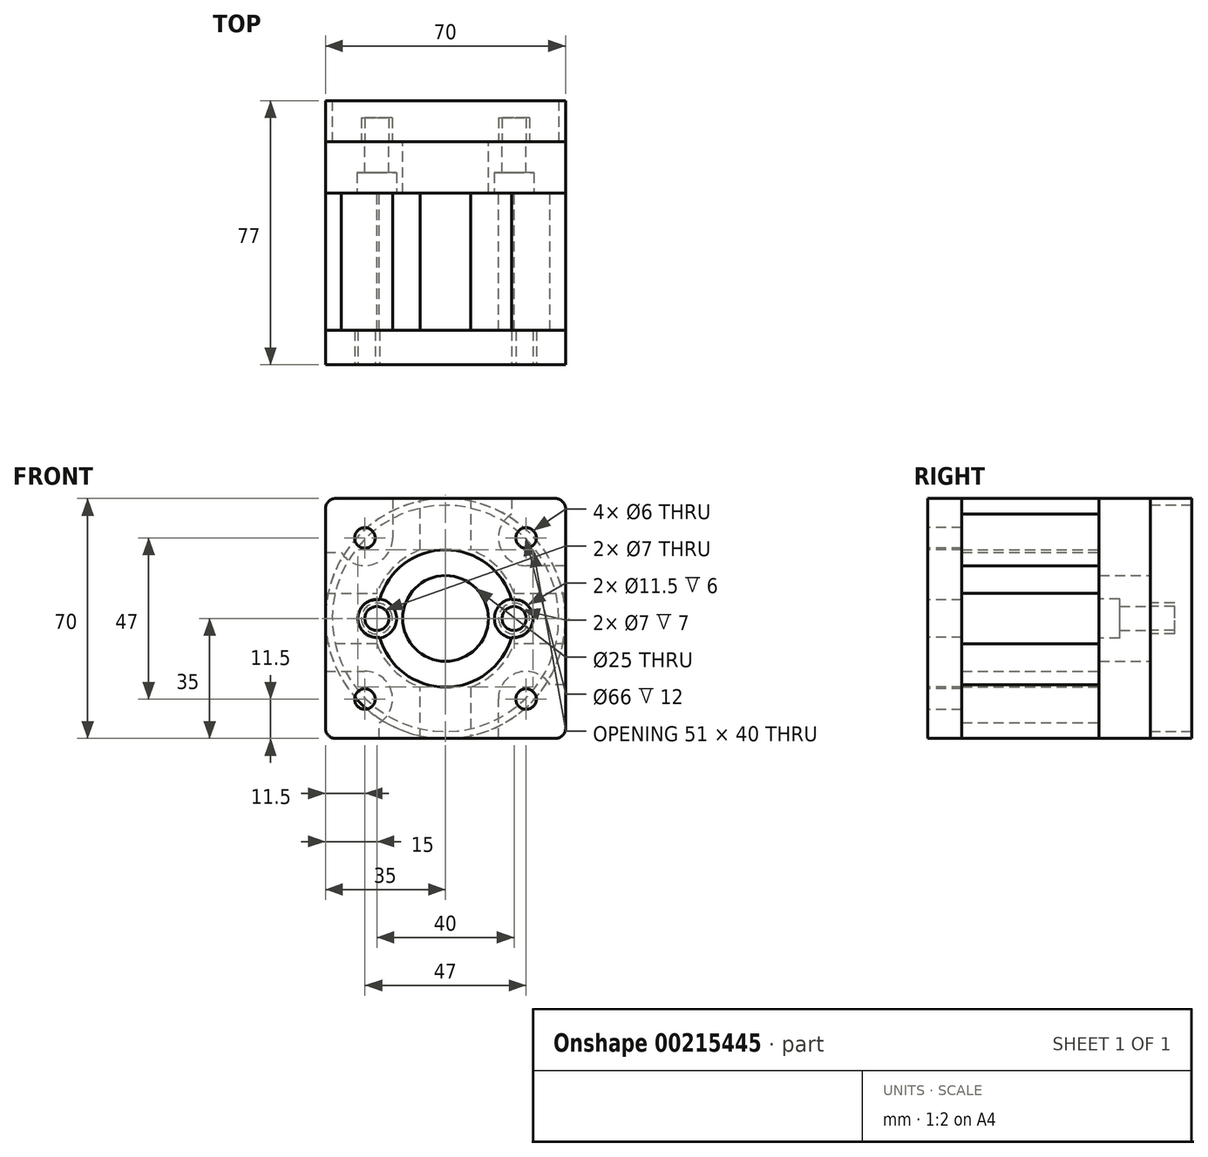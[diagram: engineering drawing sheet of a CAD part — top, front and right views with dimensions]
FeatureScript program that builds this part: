
annotation { "Feature Type Name" : "Feature", "Feature Type Description" : "" }
export const myFeature = defineFeature(function(context is Context, id is Id, definition is map)
    precondition{}
    {
        {
            var Q0;
            Q0=qCreatedBy(makeId("Front.planeOp"),FACE);
            var sketch = newSketch(context, id + "F0", { "sketchPlane" : qUnion([Q0])});
            skCircle(sketch, "E0", {"center": v(-20, 0) * mm, "radius": 4.5 * mm});
            skCircle(sketch, "E1", {"center": v(20, 0) * mm, "radius": 4.5 * mm});
            skCircle(sketch, "E2", {"center": v(-20, 0) * mm, "radius": 3.5 * mm});
            skCircle(sketch, "E3", {"center": v(20, 0) * mm, "radius": 3.5 * mm});
            skSolve(sketch);
        }
        {
            var Q0;
            Q0=makeQuery(id+"F0.imprint","IMPRINT",FACE,{"disambiguationData":[TD([[makeQuery(id+"F0.imprint","IMPRINT",EDGE,{"derivedFrom":sQuery(id+"F0.wireOp",EDGE,"E0")}),1.0]])]});
            var Q1;
            Q1=makeQuery(id+"F0.imprint","IMPRINT",FACE,{"disambiguationData":[TD([[makeQuery(id+"F0.imprint","IMPRINT",EDGE,{"derivedFrom":sQuery(id+"F0.wireOp",EDGE,"E1")}),1.0]])]});
            var Q2;
            Q2=sQuery(id+"F0.wireOp",EDGE,"E0");
            var Q3;
            Q3=sQuery(id+"F0.wireOp",EDGE,"E2");
            var Q4;
            Q4=sQuery(id+"F0.wireOp",EDGE,"E3");
            var Q5;
            Q5=sQuery(id+"F0.wireOp",EDGE,"E1");
            extrude(context, id + "F1", {"entities" : qUnion([Q0, Q1]), "surfaceEntities" : qUnion([Q2, Q3, Q4, Q5]), "oppositeDirection" : true, "depth" : 7 * mm});
        }
        {
            var Q0;
            Q0=qCreatedBy(makeId("Front.planeOp"),FACE);
            var sketch = newSketch(context, id + "F2", { "sketchPlane" : qUnion([Q0])});
            skCircle(sketch, "E4", {"center": v(0, 0) * mm, "radius": 35 * mm});
            skCircle(sketch, "E5", {"center": v(0, 0) * mm, "radius": 33 * mm});
            skSolve(sketch);
        }
        {
            var Q0;
            Q0=makeQuery(id+"F2.imprint","IMPRINT",FACE,{"disambiguationData":[TD([[makeQuery(id+"F2.imprint","IMPRINT",EDGE,{"derivedFrom":sQuery(id+"F2.wireOp",EDGE,"E4")}),1.0]])]});
            var Q1;
            Q1=sQuery(id+"F2.wireOp",EDGE,"E4");
            var Q2;
            Q2=sQuery(id+"F2.wireOp",EDGE,"E5");
            extrude(context, id + "F3", {"entities" : qUnion([Q0]), "surfaceEntities" : qUnion([Q1, Q2]), "oppositeDirection" : true, "depth" : 12 * mm});
        }
        {
            var Q0;
            Q0=qCreatedBy(makeId("Front.planeOp"),FACE);
            var sketch = newSketch(context, id + "F4", { "sketchPlane" : qUnion([Q0])});
            skLineSegment(sketch, "E6.bottom", {"start": v(-35, 35) * mm, "end": v(35, 35) * mm});
            skLineSegment(sketch, "E6.top", {"start": v(-35, -35) * mm, "end": v(35, -35) * mm});
            skLineSegment(sketch, "E6.left", {"start": v(-35, 35) * mm, "end": v(-35, -35) * mm});
            skLineSegment(sketch, "E6.right", {"start": v(35, 35) * mm, "end": v(35, -35) * mm});
            skCircle(sketch, "E7", {"center": v(0, 0) * mm, "radius": 12.5 * mm});
            skCircle(sketch, "E8", {"center": v(20, 0) * mm, "radius": 3.5 * mm});
            skCircle(sketch, "E9", {"center": v(-20, 0) * mm, "radius": 3.5 * mm});
            skSolve(sketch);
        }
        {
            var Q0;
            Q0=qSketchRegion(id+"F4",true);
            extrude(context, id + "F5", {"entities" : qUnion([Q0]), "depth" : 15 * mm});
        }
        {
            var Q0;
            Q0=qCreatedBy(makeId("Front.planeOp"),FACE);
            cPlane(context, id + "F6", {"entities" : qUnion([Q0]), "cplaneType" : CPlaneType.OFFSET, "offset" : 15 * mm, "width" : 150 * mm, "height" : 150 * mm});
        }
        {
            var Q0;
            Q0=qCreatedBy(id+"F6.planeOp",FACE);
            var sketch = newSketch(context, id + "F7", { "sketchPlane" : qUnion([Q0])});
            skCircle(sketch, "E10", {"center": v(-20, 0) * mm, "radius": 5.75 * mm});
            skCircle(sketch, "E11", {"center": v(20, 0) * mm, "radius": 5.75 * mm});
            skSolve(sketch);
        }
        {
            var Q0;
            Q0=qSketchRegion(id+"F7",true);
            extrude(context, id + "F8", {"entities" : qUnion([Q0]), "operationType" : NewBodyOperationType.REMOVE, "oppositeDirection" : true, "depth" : 6 * mm});
        }
        {
            var Q0;
            Q0=qCreatedBy(makeId("Front.planeOp"),FACE);
            cPlane(context, id + "F9", {"entities" : qUnion([Q0]), "cplaneType" : CPlaneType.OFFSET, "offset" : 65 * mm, "width" : 150 * mm, "height" : 150 * mm});
        }
        {
            var Q0;
            Q0=qCreatedBy(id+"F9.planeOp",FACE);
            var sketch = newSketch(context, id + "F10", { "sketchPlane" : qUnion([Q0])});
            skLineSegment(sketch, "E12.bottom", {"start": v(-35, 35) * mm, "end": v(35, 35) * mm});
            skLineSegment(sketch, "E12.top", {"start": v(-35, -35) * mm, "end": v(35, -35) * mm});
            skLineSegment(sketch, "E12.left", {"start": v(-35, 35) * mm, "end": v(-35, -35) * mm});
            skLineSegment(sketch, "E12.right", {"start": v(35, 35) * mm, "end": v(35, -35) * mm});
            skCircle(sketch, "E13", {"center": v(0, 0) * mm, "radius": 20 * mm});
            skCircle(sketch, "E14", {"center": v(-23.5, 23.5) * mm, "radius": 3 * mm});
            skCircle(sketch, "E15", {"center": v(23.5, 23.5) * mm, "radius": 3 * mm});
            skCircle(sketch, "E16", {"center": v(-23.5, -23.5) * mm, "radius": 3 * mm});
            skCircle(sketch, "E17", {"center": v(23.5, -23.5) * mm, "radius": 3 * mm});
            skCircle(sketch, "E18", {"center": v(-20, 0) * mm, "radius": 5.5 * mm});
            skCircle(sketch, "E19", {"center": v(20, 0) * mm, "radius": 5.5 * mm});
            skSolve(sketch);
        }
        {
            var Q0;
            Q0=qSketchRegion(id+"F10",true);
            extrude(context, id + "F11", {"entities" : qUnion([Q0]), "oppositeDirection" : true, "depth" : 10 * mm});
        }
        {
            var Q0;
            Q0=qCreatedBy(id+"F6.planeOp",FACE);
            var sketch = newSketch(context, id + "F12", { "sketchPlane" : qUnion([Q0])});
            skArc(sketch, "E20", {"start": v(-15.4, 23.5) * mm, "mid": v(-21.31, 15.7) * mm, "end": v(-30.4, 19.28) * mm});
            skLineSegment(sketch, "E21", {"start": v(-35, 19.28) * mm, "end": v(-30.4, 19.28) * mm});
            skPoint(sketch, "E22.center", {"position": v(0, 0) * mm});
            skLineSegment(sketch, "E23", {"start": v(-7.4, 20) * mm, "end": v(-7.4, 35) * mm});
            skLineSegment(sketch, "E24", {"start": v(-7.4, 35) * mm, "end": v(-15.4, 35) * mm});
            skLineSegment(sketch, "E25", {"start": v(-15.4, 35) * mm, "end": v(-15.4, 23.5) * mm});
            skLineSegment(sketch, "E26", {"start": v(-35, 7.4) * mm, "end": v(-20, 7.4) * mm});
            skLineSegment(sketch, "E27", {"start": v(-35, 19.28) * mm, "end": v(-35, 7.4) * mm});
            skArc(sketch, "E28", {"start": v(-7.4, 20) * mm, "mid": v(-15.07, 15.07) * mm, "end": v(-20, 7.4) * mm});
            skLineSegment(sketch, "E29.1.0", {"start": v(-35, -7.4) * mm, "end": v(-35, -15.4) * mm});
            skLineSegment(sketch, "E29.1.1", {"start": v(-20, -7.4) * mm, "end": v(-35, -7.4) * mm});
            skArc(sketch, "E29.1.2", {"start": v(-20, -7.4) * mm, "mid": v(-15.07, -15.07) * mm, "end": v(-7.4, -20) * mm});
            skLineSegment(sketch, "E29.1.3", {"start": v(-7.4, -35) * mm, "end": v(-7.4, -20) * mm});
            skLineSegment(sketch, "E29.1.4", {"start": v(-19.28, -35) * mm, "end": v(-7.4, -35) * mm});
            skLineSegment(sketch, "E29.1.5", {"start": v(-19.28, -35) * mm, "end": v(-19.28, -30.4) * mm});
            skArc(sketch, "E29.1.6", {"start": v(-23.5, -15.4) * mm, "mid": v(-15.7, -21.31) * mm, "end": v(-19.28, -30.4) * mm});
            skLineSegment(sketch, "E29.1.7", {"start": v(-35, -15.4) * mm, "end": v(-23.5, -15.4) * mm});
            skLineSegment(sketch, "E29.2.0", {"start": v(7.4, -35) * mm, "end": v(15.4, -35) * mm});
            skLineSegment(sketch, "E29.2.1", {"start": v(7.4, -20) * mm, "end": v(7.4, -35) * mm});
            skArc(sketch, "E29.2.2", {"start": v(7.4, -20) * mm, "mid": v(15.07, -15.07) * mm, "end": v(20, -7.4) * mm});
            skLineSegment(sketch, "E29.2.3", {"start": v(35, -7.4) * mm, "end": v(20, -7.4) * mm});
            skLineSegment(sketch, "E29.2.4", {"start": v(35, -19.28) * mm, "end": v(35, -7.4) * mm});
            skLineSegment(sketch, "E29.2.5", {"start": v(35, -19.28) * mm, "end": v(30.4, -19.28) * mm});
            skArc(sketch, "E29.2.6", {"start": v(15.4, -23.5) * mm, "mid": v(21.31, -15.7) * mm, "end": v(30.4, -19.28) * mm});
            skLineSegment(sketch, "E29.2.7", {"start": v(15.4, -35) * mm, "end": v(15.4, -23.5) * mm});
            skLineSegment(sketch, "E29.3.0", {"start": v(35, 7.4) * mm, "end": v(35, 15.4) * mm});
            skLineSegment(sketch, "E29.3.1", {"start": v(20, 7.4) * mm, "end": v(35, 7.4) * mm});
            skArc(sketch, "E29.3.2", {"start": v(20, 7.4) * mm, "mid": v(15.07, 15.07) * mm, "end": v(7.4, 20) * mm});
            skLineSegment(sketch, "E29.3.3", {"start": v(7.4, 35) * mm, "end": v(7.4, 20) * mm});
            skLineSegment(sketch, "E29.3.4", {"start": v(19.28, 35) * mm, "end": v(7.4, 35) * mm});
            skLineSegment(sketch, "E29.3.5", {"start": v(19.28, 35) * mm, "end": v(19.28, 30.4) * mm});
            skArc(sketch, "E29.3.6", {"start": v(23.5, 15.4) * mm, "mid": v(15.7, 21.31) * mm, "end": v(19.28, 30.4) * mm});
            skLineSegment(sketch, "E29.3.7", {"start": v(35, 15.4) * mm, "end": v(23.5, 15.4) * mm});
            skSolve(sketch);
        }
        {
            var Q0;
            Q0 = qSketchRegion(id + "F12", true);
            extrude(context, id + "F13", {"entities" : qUnion([Q0]), "depth" : 40 * mm});
        }
        {
            var Q0;
            Q0=makeQuery(id+"F11.opExtrude","SWEPT_EDGE",EDGE,{"disambiguationData":[OSD([sQuery(id+"F10.wireOp",EDGE,"E12.bottom"),sQuery(id+"F10.wireOp",EDGE,"E12.left")])]});
            var Q1;
            Q1=makeQuery(id+"F11.opExtrude","SWEPT_EDGE",EDGE,{"disambiguationData":[OSD([sQuery(id+"F10.wireOp",EDGE,"E12.bottom"),sQuery(id+"F10.wireOp",EDGE,"E12.right")])]});
            var Q2;
            Q2=makeQuery(id+"F11.opExtrude","SWEPT_EDGE",EDGE,{"disambiguationData":[OSD([sQuery(id+"F10.wireOp",EDGE,"E12.top"),sQuery(id+"F10.wireOp",EDGE,"E12.right")])]});
            var Q3;
            Q3=makeQuery(id+"F11.opExtrude","SWEPT_EDGE",EDGE,{"disambiguationData":[OSD([sQuery(id+"F10.wireOp",EDGE,"E12.top"),sQuery(id+"F10.wireOp",EDGE,"E12.left")])]});
            fillet(context, id + "F14", {"entities" : qUnion([Q0, Q1, Q2, Q3]), "radius" : 3 * mm, "tangentPropagation" : true, "allowEdgeOverflow" : false});
        }
        {
            var Q0;
            Q0=makeQuery(id+"F5.opExtrude","SWEPT_EDGE",EDGE,{"disambiguationData":[OSD([sQuery(id+"F4.wireOp",EDGE,"E6.top"),sQuery(id+"F4.wireOp",EDGE,"E6.right")])]});
            var Q1;
            Q1=makeQuery(id+"F5.opExtrude","SWEPT_EDGE",EDGE,{"disambiguationData":[OSD([sQuery(id+"F4.wireOp",EDGE,"E6.bottom"),sQuery(id+"F4.wireOp",EDGE,"E6.right")])]});
            var Q2;
            Q2=makeQuery(id+"F5.opExtrude","SWEPT_EDGE",EDGE,{"disambiguationData":[OSD([sQuery(id+"F4.wireOp",EDGE,"E6.bottom"),sQuery(id+"F4.wireOp",EDGE,"E6.left")])]});
            var Q3;
            Q3=makeQuery(id+"F5.opExtrude","SWEPT_EDGE",EDGE,{"disambiguationData":[OSD([sQuery(id+"F4.wireOp",EDGE,"E6.top"),sQuery(id+"F4.wireOp",EDGE,"E6.left")])]});
            fillet(context, id + "F15", {"entities" : qUnion([Q0, Q1, Q2, Q3]), "radius" : 3 * mm, "tangentPropagation" : true, "allowEdgeOverflow" : false});
        }
    });
